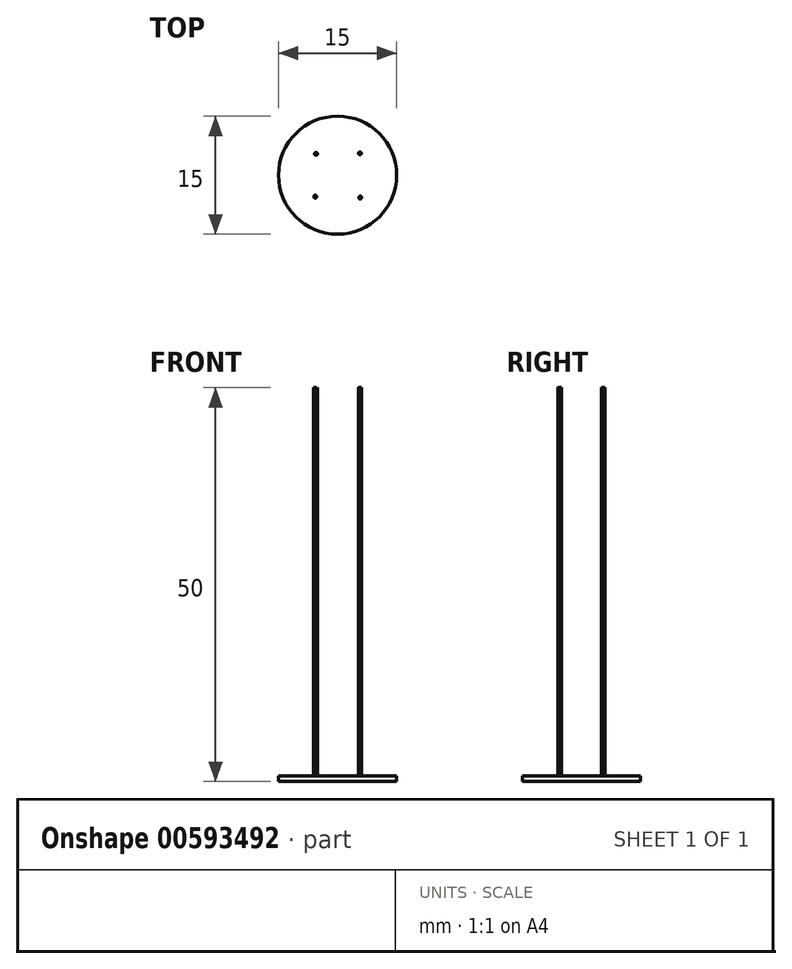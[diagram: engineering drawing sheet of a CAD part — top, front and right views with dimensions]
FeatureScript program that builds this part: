
annotation { "Feature Type Name" : "Feature", "Feature Type Description" : "" }
export const myFeature = defineFeature(function(context is Context, id is Id, definition is map)
    precondition{}
    {
        {
            var Q0;
            Q0=qCreatedBy(makeId("Top.planeOp"),FACE);
            var sketch = newSketch(context, id + "F0", { "sketchPlane" : qUnion([Q0])});
            skCircle(sketch, "E0", {"center": v(0, 0) * mm, "radius": 7.5 * mm});
            skSolve(sketch);
        }
        {
            var Q0;
            Q0=makeQuery(id+"F0.imprint","IMPRINT",FACE,{"disambiguationData":[TD([[makeQuery(id+"F0.imprint","IMPRINT",EDGE,{"derivedFrom":sQuery(id+"F0.wireOp",EDGE,"E0")}),1.0]])]});
            extrude(context, id + "F1", {"entities" : qUnion([Q0]), "depth" : 0.7 * mm, "offsetDistance" : 25.4 * mm});
        }
        {
            var Q0;
            Q0=qCreatedBy(makeId("Top.planeOp"),FACE);
            var sketch = newSketch(context, id + "F2", { "sketchPlane" : qUnion([Q0])});
            skCircle(sketch, "E1", {"center": v(-2.73, 2.72) * mm, "radius": 0.18 * mm});
            skCircle(sketch, "E2", {"center": v(2.84, 2.79) * mm, "radius": 0.18 * mm});
            skCircle(sketch, "E3", {"center": v(2.88, -2.83) * mm, "radius": 0.18 * mm});
            skCircle(sketch, "E4", {"center": v(-2.84, -2.72) * mm, "radius": 0.18 * mm});
            skSolve(sketch);
        }
        {
            var Q0;
            Q0 = qSketchRegion(id + "F2", true);
            extrude(context, id + "F3", {"entities" : qUnion([Q0]), "operationType" : NewBodyOperationType.ADD, "depth" : 50 * mm, "offsetDistance" : 25.4 * mm});
        }
    });
